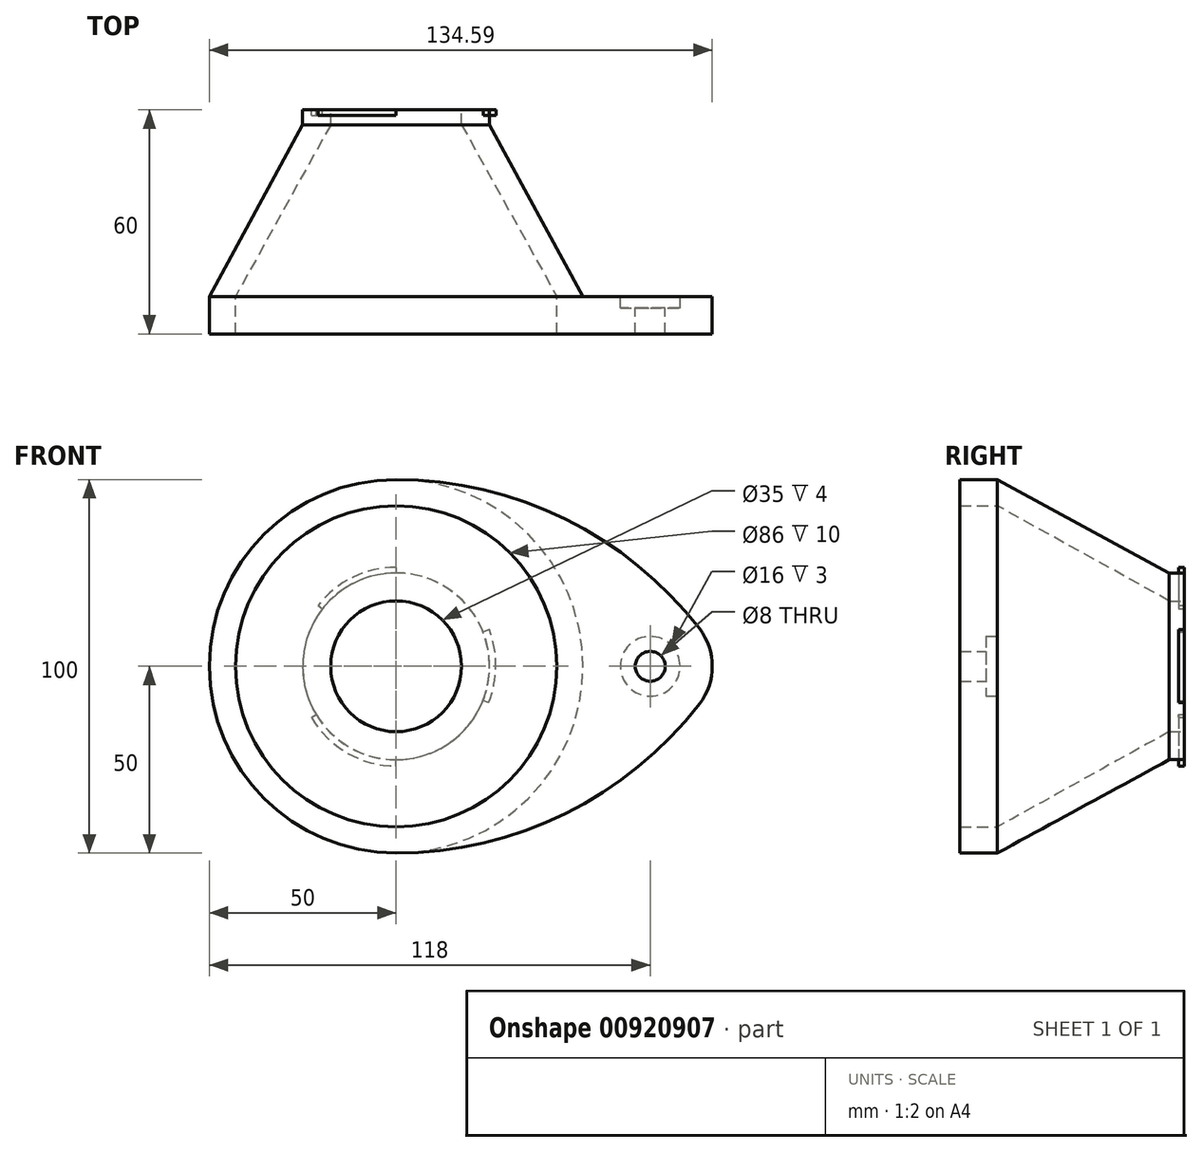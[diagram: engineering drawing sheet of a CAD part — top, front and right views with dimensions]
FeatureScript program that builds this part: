
annotation { "Feature Type Name" : "Feature", "Feature Type Description" : "" }
export const myFeature = defineFeature(function(context is Context, id is Id, definition is map)
    precondition{}
    {
        {
            var Q0;
            Q0=qCreatedBy(makeId("Front.planeOp"),FACE);
            var sketch = newSketch(context, id + "F0", { "sketchPlane" : qUnion([Q0])});
            skCircle(sketch, "E0", {"center": v(0, 0) * mm, "radius": 25 * mm});
            skArc(sketch, "E1", {"start": v(0, 26.5) * mm, "mid": v(-11.63, 23.81) * mm, "end": v(-20.9, 16.3) * mm});
            skArc(sketch, "E2", {"start": v(24.73, -9.74) * mm, "mid": v(26.69, 0) * mm, "end": v(24.91, 9.79) * mm});
            skArc(sketch, "E3", {"start": v(-22.68, -13.7) * mm, "mid": v(-13.06, -23.2) * mm, "end": v(0, -26.72) * mm});
            skLineSegment(sketch, "E4", {"start": v(-20.9, 16.3) * mm, "end": v(-19.71, 15.38) * mm});
            skLineSegment(sketch, "E5", {"start": v(0, 26.5) * mm, "end": v(0, 25) * mm});
            skLineSegment(sketch, "E6", {"start": v(24.91, 9.79) * mm, "end": v(23.27, 9.14) * mm});
            skLineSegment(sketch, "E7", {"start": v(24.73, -9.74) * mm, "end": v(23.26, -9.16) * mm});
            skLineSegment(sketch, "E8", {"start": v(0, -26.72) * mm, "end": v(0, -25) * mm});
            skLineSegment(sketch, "E9", {"start": v(-22.68, -13.7) * mm, "end": v(-21.4, -12.92) * mm});
            skCircle(sketch, "E10", {"center": v(0, 0) * mm, "radius": 17.5 * mm});
            skSolve(sketch);
        }
        {
            var Q0;
            Q0=qSketchRegion(id+"F0",true);
            extrude(context, id + "F1", {"entities" : qUnion([Q0]), "depth" : 1.5 * mm, "offsetDistance" : 25 * mm});
        }
        {
            var Q0;
            Q0=makeQuery(id+"F1.opExtrude","CAP_FACE",FACE,{"disambiguationData":[OSD([sQuery(id+"F0.wireOp",EDGE,"E0"),sQuery(id+"F0.wireOp",EDGE,"E1"),sQuery(id+"F0.wireOp",EDGE,"E2"),sQuery(id+"F0.wireOp",EDGE,"E3"),sQuery(id+"F0.wireOp",EDGE,"E4"),sQuery(id+"F0.wireOp",EDGE,"E5"),sQuery(id+"F0.wireOp",EDGE,"E6"),sQuery(id+"F0.wireOp",EDGE,"E7"),sQuery(id+"F0.wireOp",EDGE,"E8"),sQuery(id+"F0.wireOp",EDGE,"E9"),sQuery(id+"F0.wireOp",EDGE,"rjy71EB8-ImHG-pkEu-g49G-hQzt3a2hd9ZZ")])],"isStart":false});
            var sketch = newSketch(context, id + "F2", { "sketchPlane" : qUnion([Q0])});
            skCircle(sketch, "E11", {"center": v(0, 0) * mm, "radius": 17.5 * mm});
            skCircle(sketch, "E12", {"center": v(0, 0) * mm, "radius": 25 * mm});
            skSolve(sketch);
        }
        {
            var Q0;
            Q0=qSketchRegion(id+"F2",true);
            extrude(context, id + "F3", {"entities" : qUnion([Q0]), "operationType" : NewBodyOperationType.ADD, "depth" : 2.5 * mm, "offsetDistance" : 25 * mm});
        }
        {
            var Q0;
            Q0=qCreatedBy(makeId("Front.planeOp"),FACE);
            cPlane(context, id + "F4", {"entities" : qUnion([Q0]), "cplaneType" : CPlaneType.OFFSET, "offset" : 50 * mm, "width" : 150 * mm, "height" : 150 * mm});
        }
        {
            var Q0;
            Q0=makeQuery(id+"F3.opExtrude","CAP_FACE",FACE,{"disambiguationData":[OSD([sQuery(id+"F2.wireOp",EDGE,"E11"),sQuery(id+"F2.wireOp",EDGE,"E12")])],"isStart":false});
            var sketch = newSketch(context, id + "F5", { "sketchPlane" : qUnion([Q0])});
            skCircle(sketch, "E13", {"center": v(0, 0) * mm, "radius": 25 * mm});
            skSolve(sketch);
        }
        {
            var Q0;
            Q0=qCreatedBy(id+"F4.planeOp",FACE);
            var sketch = newSketch(context, id + "F6", { "sketchPlane" : qUnion([Q0])});
            skCircle(sketch, "E14", {"center": v(0, 0) * mm, "radius": 50 * mm});
            skSolve(sketch);
        }
        {
            var Q1;
            Q1=qSketchRegion(id+"F6",true);
            var Q2;
            Q2=qSketchRegion(id+"F5",true);
            loft(context, id + "F7", {"operationType" : NewBodyOperationType.ADD, "sheetProfilesArray" : [{ "sheetProfileEntities" : qUnion([Q1]) }, { "sheetProfileEntities" : qUnion([Q2]) }]});
        }
        {
            var Q0;
            Q0=makeQuery(id+"F7.opLoft","CAP_FACE",FACE,{"disambiguationData":[OSD([makeQuery(id+"F6.imprint","IMPRINT",FACE,{"disambiguationData":[TD([[makeQuery(id+"F6.imprint","IMPRINT",EDGE,{"derivedFrom":sQuery(id+"F6.wireOp",EDGE,"E14")}),1.0]])]})])],"isStart":true});
            var sketch = newSketch(context, id + "F8", { "sketchPlane" : qUnion([Q0])});
            skCircle(sketch, "E15", {"center": v(0, 0) * mm, "radius": 43 * mm});
            skSolve(sketch);
        }
        {
            var Q0;
            Q0=makeQuery(id+"F7.opLoft","CAP_FACE",FACE,{"disambiguationData":[OSD([makeQuery(id+"F5.imprint","IMPRINT",FACE,{"disambiguationData":[TD([[makeQuery(id+"F5.imprint","IMPRINT",EDGE,{"derivedFrom":makeQuery(id+"F3.opExtrude","CAP_EDGE",EDGE,{"disambiguationData":[OSD([sQuery(id+"F2.wireOp",EDGE,"E11")])],"isStart":false})}),1.0]])]})])],"isStart":true});
            var sketch = newSketch(context, id + "F9", { "sketchPlane" : qUnion([Q0])});
            skCircle(sketch, "E16", {"center": v(0, 0) * mm, "radius": 17.5 * mm});
            skSolve(sketch);
        }
        {
            var Q1;
            Q1=qSketchRegion(id+"F9",true);
            var Q2;
            Q2=qSketchRegion(id+"F8",true);
            loft(context, id + "F10", {"operationType" : NewBodyOperationType.REMOVE, "sheetProfilesArray" : [{ "sheetProfileEntities" : qUnion([Q1]) }, { "sheetProfileEntities" : qUnion([Q2]) }]});
        }
        {
            var Q0;
            Q0=makeQuery(id+"F7.opLoft","CAP_FACE",FACE,{"disambiguationData":[OSD([makeQuery(id+"F6.imprint","IMPRINT",FACE,{"disambiguationData":[TD([[makeQuery(id+"F6.imprint","IMPRINT",EDGE,{"derivedFrom":sQuery(id+"F6.wireOp",EDGE,"E14")}),1.0]])]})])],"isStart":true});
            var sketch = newSketch(context, id + "F11", { "sketchPlane" : qUnion([Q0])});
            skCircle(sketch, "E17", {"center": v(0, 0) * mm, "radius": 43 * mm});
            skCircle(sketch, "E18", {"center": v(0, 0) * mm, "radius": 50 * mm});
            skSolve(sketch);
        }
        {
            var Q0;
            Q0=qSketchRegion(id+"F11",true);
            extrude(context, id + "F12", {"entities" : qUnion([Q0]), "operationType" : NewBodyOperationType.ADD, "depth" : 10 * mm, "offsetDistance" : 25 * mm});
        }
        {
            var Q0;
            Q0=makeQuery(id+"F12.opExtrude","CAP_FACE",FACE,{"disambiguationData":[OSD([sQuery(id+"F11.wireOp",EDGE,"E17"),sQuery(id+"F11.wireOp",EDGE,"E18")])],"isStart":false});
            var sketch = newSketch(context, id + "F13", { "sketchPlane" : qUnion([Q0])});
            skCircle(sketch, "E19", {"center": v(0, 0) * mm, "radius": 43 * mm});
            skCircle(sketch, "E20", {"center": v(0, 0) * mm, "radius": 50 * mm});
            skLineSegment(sketch, "E21.bottom", {"start": v(0, 50) * mm, "end": v(100, 50) * mm});
            skLineSegment(sketch, "E21.top", {"start": v(0, -50) * mm, "end": v(100, -50) * mm});
            skLineSegment(sketch, "E21.right", {"start": v(100, 50) * mm, "end": v(100, -50) * mm});
            skPoint(sketch, "E21.middle", {"position": v(50, 0) * mm});
            skLineSegment(sketch, "E22", {"start": v(100, -50) * mm, "end": v(100, 50) * mm});
            skSolve(sketch);
        }
        {
            var Q0;
            Q0 = qSketchRegion(id + "F13", true);
            extrude(context, id + "F14", {"entities" : qUnion([Q0]), "operationType" : NewBodyOperationType.ADD, "oppositeDirection" : true, "depth" : 10 * mm, "offsetDistance" : 25 * mm});
        }
        {
            var Q0;
            Q0=makeQuery(id+"F14.opExtrude","CAP_FACE",FACE,{"disambiguationData":[OSD([sQuery(id+"F13.wireOp",EDGE,"E19"),sQuery(id+"F13.wireOp",EDGE,"E20"),sQuery(id+"F13.wireOp",EDGE,"E21.bottom"),sQuery(id+"F13.wireOp",EDGE,"E21.top"),sQuery(id+"F13.wireOp",EDGE,"E22")])],"isStart":false});
            var sketch = newSketch(context, id + "F15", { "sketchPlane" : qUnion([Q0])});
            skCircle(sketch, "E23", {"center": v(-68, 0) * mm, "radius": 8 * mm});
            skSolve(sketch);
        }
        {
            var Q0;
            Q0 = qSketchRegion(id + "F15", true);
            extrude(context, id + "F16", {"entities" : qUnion([Q0]), "operationType" : NewBodyOperationType.REMOVE, "oppositeDirection" : true, "depth" : 3 * mm, "offsetDistance" : 25 * mm});
        }
        {
            var Q0;
            Q0=makeQuery(id+"F16.boolean.opBoolean","COPY",FACE,{"derivedFrom":makeQuery(id+"F16.opExtrude","CAP_FACE",FACE,{"disambiguationData":[OSD([sQuery(id+"F15.wireOp",EDGE,"E23")])],"isStart":false})});
            var sketch = newSketch(context, id + "F17", { "sketchPlane" : qUnion([Q0])});
            skCircle(sketch, "E24", {"center": v(-68, 0) * mm, "radius": 4 * mm});
            skSolve(sketch);
        }
        {
            var Q0;
            Q0 = qSketchRegion(id + "F17", true);
            extrude(context, id + "F18", {"entities" : qUnion([Q0]), "operationType" : NewBodyOperationType.REMOVE, "oppositeDirection" : true, "depth" : 25 * mm, "offsetDistance" : 25 * mm});
        }
        {
            var Q0;
            Q0=makeQuery(id+"F14.opExtrude","CAP_FACE",FACE,{"disambiguationData":[OSD([sQuery(id+"F13.wireOp",EDGE,"E19"),sQuery(id+"F13.wireOp",EDGE,"E20"),sQuery(id+"F13.wireOp",EDGE,"E21.bottom"),sQuery(id+"F13.wireOp",EDGE,"E21.top"),sQuery(id+"F13.wireOp",EDGE,"E22")])],"isStart":false});
            var sketch = newSketch(context, id + "F19", { "sketchPlane" : qUnion([Q0])});
            skLineSegment(sketch, "E25", {"start": v(0, 1.28) * mm, "end": v(-88, 0) * mm, "construction": true});
            skArc(sketch, "E26", {"start": v(-88, 0) * mm, "mid": v(-50.6, -36.63) * mm, "end": v(0, -50) * mm});
            skArc(sketch, "E27", {"start": v(0, 50) * mm, "mid": v(-50.6, 36.63) * mm, "end": v(-88, 0) * mm});
            skLineSegment(sketch, "E28", {"start": v(0, 50) * mm, "end": v(0, 63.02) * mm});
            skLineSegment(sketch, "E29", {"start": v(0, 63.02) * mm, "end": v(-105.39, 63.02) * mm});
            skLineSegment(sketch, "E30", {"start": v(-105.39, 63.02) * mm, "end": v(-106.7, -65.55) * mm});
            skLineSegment(sketch, "E31", {"start": v(-106.7, -65.55) * mm, "end": v(0, -50) * mm});
            skSolve(sketch);
        }
        {
            var Q0;
            Q0 = qSketchRegion(id + "F19", true);
            extrude(context, id + "F20", {"entities" : qUnion([Q0]), "operationType" : NewBodyOperationType.REMOVE, "oppositeDirection" : true, "depth" : 25 * mm, "offsetDistance" : 25 * mm});
        }
        {
            var Q0;
            Q0=makeQuery(id+"F20.boolean.opBoolean","COPY",EDGE,{"derivedFrom":makeQuery(id+"F20.opExtrude","SWEPT_EDGE",EDGE,{"disambiguationData":[OSD([sQuery(id+"F19.wireOp",EDGE,"E26"),sQuery(id+"F19.wireOp",EDGE,"E27")])]})});
            fillet(context, id + "F21", {"entities" : qUnion([Q0]), "radius" : 16.46 * mm, "tangentPropagation" : true, "allowEdgeOverflow" : false});
        }
    });
